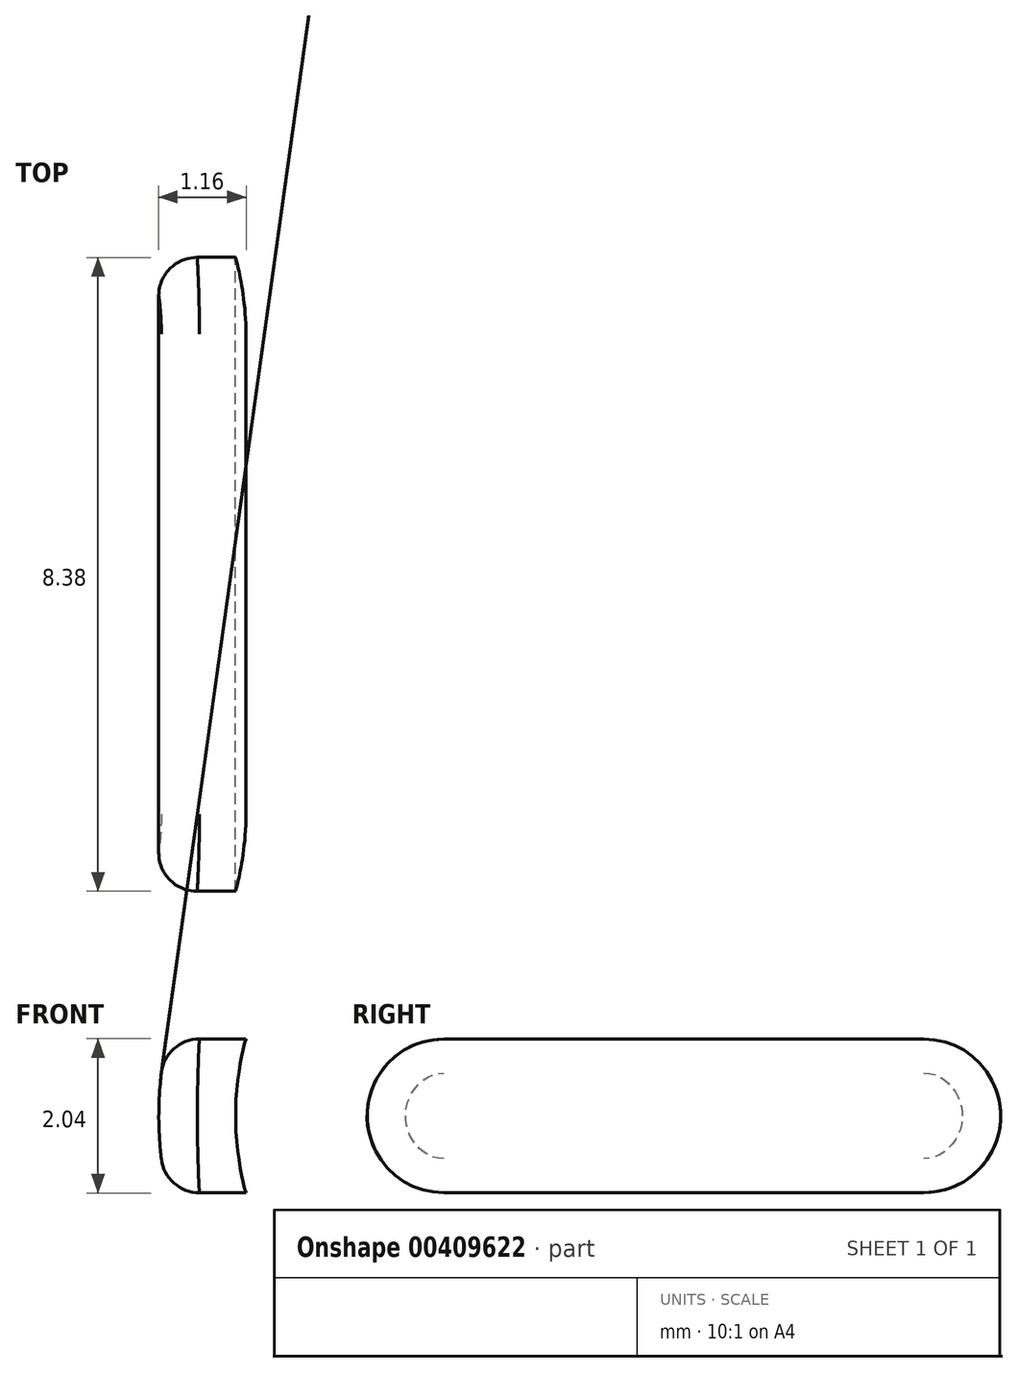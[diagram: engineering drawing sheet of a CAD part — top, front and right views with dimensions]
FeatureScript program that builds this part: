
annotation { "Feature Type Name" : "Feature", "Feature Type Description" : "" }
export const myFeature = defineFeature(function(context is Context, id is Id, definition is map)
    precondition{}
    {
        {
            var Q0;
            Q0=qCreatedBy(makeId("Front.planeOp"),FACE);
            var sketch = newSketch(context, id + "F0", { "sketchPlane" : qUnion([Q0])});
            skArc(sketch, "E0", {"start": v(-3.67, 1.02) * mm, "mid": v(-3.81, 0) * mm, "end": v(-3.67, -1.02) * mm});
            skArc(sketch, "E1.0", {"start": v(-4.72, 1.02) * mm, "mid": v(-4.83, 0) * mm, "end": v(-4.72, -1.02) * mm});
            skLineSegment(sketch, "E2", {"start": v(-3.67, -1.02) * mm, "end": v(-4.72, -1.02) * mm});
            skLineSegment(sketch, "E3", {"start": v(-3.67, 1.02) * mm, "end": v(-4.72, 1.02) * mm});
            skSolve(sketch);
        }
        {
            var Q0;
            Q0 = qSketchRegion(id + "F0", true);
            extrude(context, id + "F1", {"entities" : qUnion([Q0]), "depth" : 12.7 * mm});
        }
        {
            var Q0;
            Q0=qCreatedBy(makeId("Right.planeOp"),FACE);
            var sketch = newSketch(context, id + "F2", { "sketchPlane" : qUnion([Q0])});
            skLineSegment(sketch, "E4", {"start": v(-12.7, 0) * mm, "end": v(-12.7, -1.02) * mm});
            skLineSegment(sketch, "E5", {"start": v(-12.7, -1.02) * mm, "end": v(0, -1.02) * mm});
            skLineSegment(sketch, "E6", {"start": v(0, -1.02) * mm, "end": v(0, 1.02) * mm});
            skLineSegment(sketch, "E7", {"start": v(0, 1.02) * mm, "end": v(-12.7, 1.02) * mm});
            skLineSegment(sketch, "E8", {"start": v(-12.7, 0) * mm, "end": v(-12.7, 1.02) * mm});
            skArc(sketch, "E9", {"start": v(-3.17, -1.02) * mm, "mid": v(-2.16, 0) * mm, "end": v(-3.17, 1.02) * mm});
            skArc(sketch, "E10", {"start": v(-9.52, 1.02) * mm, "mid": v(-10.54, 0) * mm, "end": v(-9.52, -1.02) * mm});
            skPoint(sketch, "E11.orphan", {"position": v(0, 0) * mm});
            skPoint(sketch, "E12.orphan", {"position": v(-6.35, 0) * mm});
            skSolve(sketch);
        }
        {
            var Q0;
            {var subQ4=sQuery(id+"F2.wireOp",EDGE,"E4");Q0=makeQuery(id+"F2.imprint","IMPRINT",FACE,{"disambiguationData":[TD([[makeQuery(id+"F2.imprint","IMPRINT",EDGE,{"derivedFrom":subQ4}),1.0]])]});}
            var Q1;
            {var subQ0=sQuery(id+"F2.wireOp",EDGE,"E6");Q1=makeQuery(id+"F2.imprint","IMPRINT",FACE,{"disambiguationData":[TD([[makeQuery(id+"F2.imprint","IMPRINT",EDGE,{"derivedFrom":subQ0}),1.0]])]});}
            extrude(context, id + "F3", {"entities" : qUnion([Q0, Q1]), "operationType" : NewBodyOperationType.REMOVE, "oppositeDirection" : true, "depth" : 25.4 * mm});
        }
        {
            var Q0;
            Q0=makeQuery(id+"F1.opExtrude","SWEPT_EDGE",EDGE,{"disambiguationData":[OSD([sQuery(id+"F0.wireOp",EDGE,"E1.0"),sQuery(id+"F0.wireOp",EDGE,"E3")])]});
            fillet(context, id + "F4", {"entities" : qUnion([Q0]), "radius" : 0.5 * mm, "tangentPropagation" : true, "allowEdgeOverflow" : false});
        }
    });
